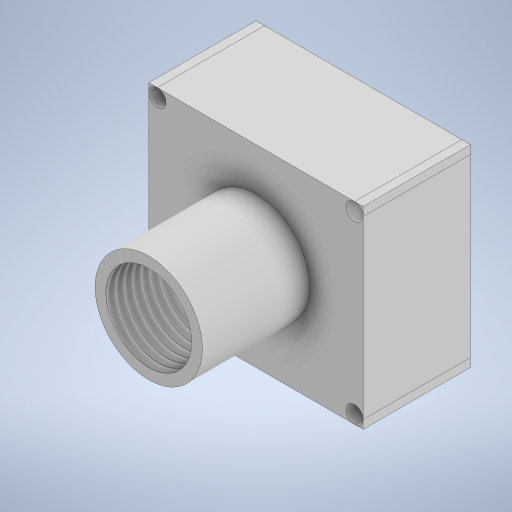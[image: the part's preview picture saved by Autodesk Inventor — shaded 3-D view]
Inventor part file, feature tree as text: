
AUTODESK INVENTOR PART (.ipt)
format: ipt  version: 2024 (Build 280153000, 153)  size: 276,480 bytes
history: native  units: in
note: dims shown in document units (in); Inventor stores cm internally (conversion verified against a paired STEP export)
features: extrude x3, sketch x3, thread x1
ambient origin geometry x8: Origin, YZ Plane, XZ Plane, XY Plane, X Axis, Y Axis, Z Axis, Center Point
bodies: Solid1 (feature_tree)
feature tree (7):
  extrude  "Extrusion1"  Depth=3.5433in
  extrude  "Extrusion2"  TaperAngle=0.0deg  [1 undecoded]
  extrude  "Extrusion3"  Depth=1.9685in TaperAngle=0.0deg
  thread  "Thread1"  [1 undecoded]
  sketch  "Sketch1"  dims[d0=3.937in d1=3.5433in]
  sketch  "Sketch2"  dims[d2=1.9685in d3=0.0in d8=0.0in d9=0.0in]
  sketch  "Sketch3"  dims[d12=1.9685in d13=0.0in d14=1.1811in d15=0.0in d10=0.0394in d11=0.0059in d16=0.8108in d17=0.0025in d18=0.0295in d19=0.0148in]
note: 2 required parameter values undecoded (feature->parameter linkage not recoverable at this tier; creation-order binding heuristic only, values carry confidence <= 0.55)
